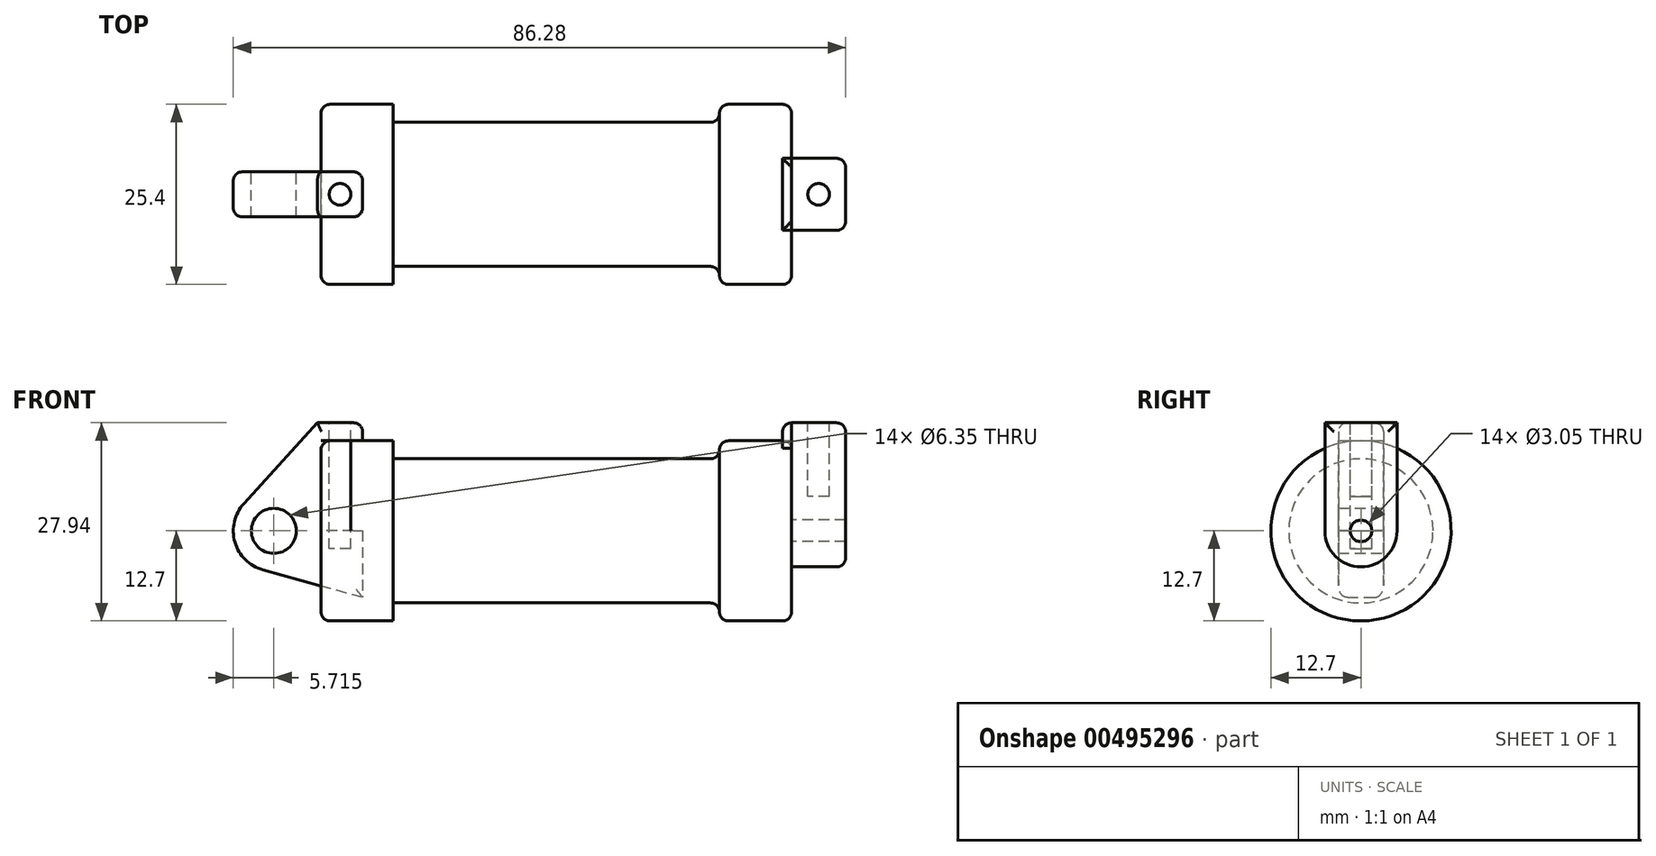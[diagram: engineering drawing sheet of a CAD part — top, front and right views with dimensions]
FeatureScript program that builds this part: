
annotation { "Feature Type Name" : "Feature", "Feature Type Description" : "" }
export const myFeature = defineFeature(function(context is Context, id is Id, definition is map)
    precondition{}
    {
        {
            var Q0;
            Q0=qCreatedBy(makeId("Front.planeOp"),FACE);
            var sketch = newSketch(context, id + "F0", { "sketchPlane" : qUnion([Q0])});
            skLineSegment(sketch, "E0", {"start": v(0, 0) * mm, "end": v(0, 12.7) * mm});
            skLineSegment(sketch, "E1", {"start": v(0, 12.7) * mm, "end": v(10.16, 12.7) * mm});
            skLineSegment(sketch, "E2", {"start": v(10.16, 12.7) * mm, "end": v(10.16, 10.16) * mm});
            skLineSegment(sketch, "E3", {"start": v(10.16, 10.16) * mm, "end": v(56.13, 10.16) * mm});
            skLineSegment(sketch, "E4", {"start": v(56.13, 10.16) * mm, "end": v(56.13, 12.7) * mm});
            skLineSegment(sketch, "E5", {"start": v(56.13, 12.7) * mm, "end": v(66.3, 12.7) * mm});
            skLineSegment(sketch, "E6", {"start": v(66.3, 12.7) * mm, "end": v(66.3, 0) * mm});
            skLineSegment(sketch, "E7", {"start": v(66.3, 0) * mm, "end": v(0, 0) * mm});
            skLineSegment(sketch, "E8", {"start": v(5.84, 15.24) * mm, "end": v(-0.5, 15.24) * mm});
            skLineSegment(sketch, "E9", {"start": v(-0.5, 15.24) * mm, "end": v(-10.88, 3.85) * mm});
            skLineSegment(sketch, "E10", {"start": v(0, 0) * mm, "end": v(-6.65, 0) * mm});
            skCircle(sketch, "E11", {"center": v(-6.65, 0) * mm, "radius": 5.72 * mm});
            skCircle(sketch, "E12", {"center": v(-6.65, 0) * mm, "radius": 3.18 * mm});
            skLineSegment(sketch, "E13", {"start": v(5.84, 15.24) * mm, "end": v(5.84, -9.4) * mm});
            skLineSegment(sketch, "E14", {"start": v(5.84, -9.4) * mm, "end": v(-8.18, -5.5) * mm});
            skSolve(sketch);
        }
        {
            var Q0;
            {var subQ0=sQuery(id+"F0.wireOp",EDGE,"E2");Q0=makeQuery(id+"F0.imprint","IMPRINT",FACE,{"disambiguationData":[TD([[makeQuery(id+"F0.imprint","IMPRINT",EDGE,{"derivedFrom":subQ0}),-1.0]])]});}
            var Q1;
            {var subQ0=sQuery(id+"F0.wireOp",EDGE,"E0");Q1=makeQuery(id+"F0.imprint","IMPRINT",FACE,{"disambiguationData":[TD([[makeQuery(id+"F0.imprint","IMPRINT",EDGE,{"derivedFrom":subQ0}),-1.0]])]});}
            var Q2;
            Q2=sQuery(id+"F0.wireOp",EDGE,"E7");
            revolve(context, id + "F1", {"entities" : qUnion([Q0, Q1]), "axis" : qUnion([Q2]), "revolveType" : RevolveType.FULL});
        }
        {
            var Q0;
            {var subQ1=sQuery(id+"F0.wireOp",EDGE,"E0");Q0=makeQuery(id+"F0.imprint","IMPRINT",FACE,{"disambiguationData":[TD([[makeQuery(id+"F0.imprint","IMPRINT",EDGE,{"derivedFrom":subQ1}),1.0]])]});}
            var Q1;
            {var subQ0=sQuery(id+"F0.wireOp",EDGE,"E14");Q1=makeQuery(id+"F0.imprint","IMPRINT",FACE,{"disambiguationData":[TD([[makeQuery(id+"F0.imprint","IMPRINT",EDGE,{"derivedFrom":subQ0}),-1.0]])]});}
            var Q2;
            {var subQ5=sQuery(id+"F0.wireOp",EDGE,"E12");Q2=makeQuery(id+"F0.imprint","IMPRINT",FACE,{"disambiguationData":[TD([[makeQuery(id+"F0.imprint","IMPRINT",EDGE,{"derivedFrom":subQ5}),-1.0]])]});}
            extrude(context, id + "F2", {"entities" : qUnion([Q0, Q1, Q2]), "endBound" : BoundingType.SYMMETRIC, "depth" : 6.35 * mm});
        }
        {
            var Q0;
            Q0=makeQuery(id+"F1.opRevolve","SWEPT_FACE",FACE,{"disambiguationData":[OSD([sQuery(id+"F0.wireOp",EDGE,"E6")])]});
            var sketch = newSketch(context, id + "F3", { "sketchPlane" : qUnion([Q0])});
            skCircle(sketch, "E15", {"center": v(0, 0) * mm, "radius": 1.52 * mm});
            skCircle(sketch, "E16", {"center": v(0, 0) * mm, "radius": 5.08 * mm});
            skLineSegment(sketch, "E17", {"start": v(-12.7, 0) * mm, "end": v(12.7, 0) * mm, "construction": true});
            skPoint(sketch, "E18", {"position": v(5.08, 0) * mm});
            skPoint(sketch, "E19", {"position": v(-5.08, 0) * mm});
            skLineSegment(sketch, "E20", {"start": v(5.08, 0) * mm, "end": v(5.08, 15.24) * mm});
            skLineSegment(sketch, "E21", {"start": v(-5.08, 0) * mm, "end": v(-5.08, 15.24) * mm});
            skLineSegment(sketch, "E22", {"start": v(-5.08, 15.24) * mm, "end": v(5.08, 15.24) * mm});
            skSolve(sketch);
        }
        {
            var Q0;
            Q0 = qSketchRegion(id + "F3", true);
            extrude(context, id + "F4", {"entities" : qUnion([Q0]), "depth" : 7.62 * mm});
        }
        {
            var Q0;
            {var subQ0=sQuery(id+"F3.wireOp",EDGE,"E22");Q0=makeQuery(id+"F3.imprint","IMPRINT",FACE,{"disambiguationData":[TD([[makeQuery(id+"F3.imprint","IMPRINT",EDGE,{"derivedFrom":subQ0}),-1.0]])]});}
            extrude(context, id + "F5", {"entities" : qUnion([Q0]), "oppositeDirection" : true, "depth" : 1.27 * mm});
        }
        {
            var Q0;
            Q0=makeQuery(id+"F4.opExtrude","SWEPT_FACE",FACE,{"disambiguationData":[OSD([sQuery(id+"F3.wireOp",EDGE,"E22")])]});
            var sketch = newSketch(context, id + "F6", { "sketchPlane" : qUnion([Q0])});
            skLineSegment(sketch, "E23", {"start": v(70.1, 5.08) * mm, "end": v(70.1, -5.08) * mm, "construction": true});
            skPoint(sketch, "E24", {"position": v(70.1, 0) * mm});
            skCircle(sketch, "E25", {"center": v(70.1, 0) * mm, "radius": 1.52 * mm});
            skSolve(sketch);
        }
        {
            var Q0;
            Q0=makeQuery(id+"F6.imprint","IMPRINT",FACE,{"disambiguationData":[TD([[makeQuery(id+"F6.imprint","IMPRINT",EDGE,{"derivedFrom":sQuery(id+"F6.wireOp",EDGE,"E25")}),1.0]])]});
            var Q1;
            Q1=sQuery(id+"F6.wireOp",EDGE,"E25");
            extrude(context, id + "F7", {"entities" : qUnion([Q0]), "surfaceEntities" : qUnion([Q1]), "oppositeDirection" : true, "depth" : 10.4 * mm});
        }
        {
            var Q0;
            Q0=makeQuery(id+"F2.opExtrude","SWEPT_FACE",FACE,{"disambiguationData":[OSD([sQuery(id+"F0.wireOp",EDGE,"E8")])]});
            var sketch = newSketch(context, id + "F8", { "sketchPlane" : qUnion([Q0])});
            skLineSegment(sketch, "E26", {"start": v(-0.5, 3.18) * mm, "end": v(5.84, -3.18) * mm, "construction": true});
            skPoint(sketch, "E27", {"position": v(2.67, 0) * mm});
            skCircle(sketch, "E28", {"center": v(2.67, 0) * mm, "radius": 1.52 * mm});
            skSolve(sketch);
        }
        {
            var Q0;
            Q0=makeQuery(id+"F8.imprint","IMPRINT",FACE,{"disambiguationData":[TD([[makeQuery(id+"F8.imprint","IMPRINT",EDGE,{"derivedFrom":sQuery(id+"F8.wireOp",EDGE,"E28")}),1.0]])]});
            var Q1;
            Q1=sQuery(id+"F8.wireOp",EDGE,"E28");
            extrude(context, id + "F9", {"entities" : qUnion([Q0]), "surfaceEntities" : qUnion([Q1]), "oppositeDirection" : true, "depth" : 17.78 * mm});
        }
        {
            var Q0;
            Q0=makeQuery(id+"F1.opRevolve","SWEPT_FACE",FACE,{"disambiguationData":[OSD([sQuery(id+"F0.wireOp",EDGE,"E6")])]});
            var Q1;
            Q1=makeQuery(id+"F1.opRevolve","SWEPT_FACE",FACE,{"disambiguationData":[OSD([sQuery(id+"F0.wireOp",EDGE,"E0")])]});
            var Q2;
            Q2=makeQuery(id+"F1.opRevolve","SWEPT_FACE",FACE,{"disambiguationData":[OSD([sQuery(id+"F0.wireOp",EDGE,"E4")])]});
            var Q3;
            Q3=makeQuery(id+"F4.opExtrude","CAP_EDGE",EDGE,{"disambiguationData":[OSD([sQuery(id+"F3.wireOp",EDGE,"E20")])],"isStart":false});
            var Q4;
            {var subQ0=sQuery(id+"F3.wireOp",EDGE,"E22");Q4=makeQuery(id+"F7.opExtrude","CAP_EDGE",EDGE,{"disambiguationData":[OSD([subQ0]),TDD([makeQuery(id+"F6.imprint","IMPRINT",EDGE,{"derivedFrom":makeQuery(id+"F4.opExtrude","CAP_EDGE",EDGE,{"disambiguationData":[OSD([subQ0])],"isStart":false})})])],"isStart":true});}
            var Q5;
            Q5=makeQuery(id+"F7.opExtrude","CAP_EDGE",EDGE,{"disambiguationData":[OSD([sQuery(id+"F3.wireOp",EDGE,"E21"),sQuery(id+"F3.wireOp",EDGE,"E22")])],"isStart":true});
            var Q6;
            Q6=makeQuery(id+"F7.opExtrude","CAP_EDGE",EDGE,{"disambiguationData":[OSD([sQuery(id+"F3.wireOp",EDGE,"E20"),sQuery(id+"F3.wireOp",EDGE,"E22")])],"isStart":true});
            var Q7;
            Q7=makeQuery(id+"F5.opExtrude","CAP_EDGE",EDGE,{"disambiguationData":[OSD([sQuery(id+"F3.wireOp",EDGE,"E22")])],"isStart":false});
            var Q8;
            Q8=makeQuery(id+"F5.opExtrude","SWEPT_EDGE",EDGE,{"disambiguationData":[OSD([sQuery(id+"F3.wireOp",EDGE,"E21"),sQuery(id+"F3.wireOp",EDGE,"E22")])]});
            var Q9;
            Q9=makeQuery(id+"F5.opExtrude","SWEPT_EDGE",EDGE,{"disambiguationData":[OSD([sQuery(id+"F3.wireOp",EDGE,"E20"),sQuery(id+"F3.wireOp",EDGE,"E22")])]});
            var Q10;
            Q10=makeQuery(id+"F2.opExtrude","CAP_EDGE",EDGE,{"disambiguationData":[OSD([sQuery(id+"F0.wireOp",EDGE,"E11")])],"isStart":true});
            var Q11;
            Q11=makeQuery(id+"F2.opExtrude","CAP_EDGE",EDGE,{"disambiguationData":[OSD([sQuery(id+"F0.wireOp",EDGE,"E9")])],"isStart":true});
            var Q12;
            Q12=makeQuery(id+"F2.opExtrude","CAP_EDGE",EDGE,{"disambiguationData":[OSD([sQuery(id+"F0.wireOp",EDGE,"E9")])],"isStart":false});
            var Q13;
            Q13=makeQuery(id+"F2.opExtrude","CAP_EDGE",EDGE,{"disambiguationData":[OSD([sQuery(id+"F0.wireOp",EDGE,"E11")])],"isStart":false});
            var Q14;
            Q14=makeQuery(id+"F2.opExtrude","CAP_EDGE",EDGE,{"disambiguationData":[OSD([sQuery(id+"F0.wireOp",EDGE,"E8")])],"isStart":true});
            var Q15;
            Q15=makeQuery(id+"F2.opExtrude","CAP_EDGE",EDGE,{"disambiguationData":[OSD([sQuery(id+"F0.wireOp",EDGE,"E8")])],"isStart":false});
            var Q16;
            Q16=makeQuery(id+"F2.opExtrude","SWEPT_EDGE",EDGE,{"disambiguationData":[OSD([sQuery(id+"F0.wireOp",EDGE,"E8"),sQuery(id+"F0.wireOp",EDGE,"E13")])]});
            var Q17;
            {var subQ0=sQuery(id+"F0.wireOp",EDGE,"E8");var subQ1=sQuery(id+"F0.wireOp",EDGE,"E13");Q17=makeQuery(id+"F9.boolean.opBoolean","MERGE",EDGE,{"derivedFrom":[makeQuery(id+"F2.opExtrude","CAP_EDGE",EDGE,{"disambiguationData":[OSD([subQ1]),TDD([makeQuery(id+"F0.imprint","IMPRINT",EDGE,{"disambiguationData":[TD([[makeQuery(id+"F0.imprint","INTERSECT",VERTEX,{"derivedFrom":[subQ0,subQ1]}),-1.0]])],"derivedFrom":subQ1})])],"isStart":false}),makeQuery(id+"F2.opExtrude","CAP_EDGE",EDGE,{"disambiguationData":[OSD([subQ1]),TDD([makeQuery(id+"F0.imprint","IMPRINT",EDGE,{"disambiguationData":[TD([[makeQuery(id+"F0.imprint","INTERSECT",VERTEX,{"derivedFrom":[subQ1,sQuery(id+"F0.wireOp",EDGE,"E14")]}),1.0]])],"derivedFrom":subQ1})])],"isStart":false}),makeQuery(id+"F9.opExtrude","SWEPT_EDGE",EDGE,{"disambiguationData":[OSD([subQ0,subQ1]),TDD([makeQuery(id+"F8.imprint","INTERSECT",VERTEX,{"derivedFrom":[makeQuery(id+"F2.opExtrude","SWEPT_EDGE",EDGE,{"disambiguationData":[OSD([subQ0,subQ1])]}),makeQuery(id+"F2.opExtrude","CAP_EDGE",EDGE,{"disambiguationData":[OSD([subQ0])],"isStart":false})]})])]})]});}
            var Q18;
            {var subQ0=sQuery(id+"F0.wireOp",EDGE,"E8");var subQ1=sQuery(id+"F0.wireOp",EDGE,"E13");Q18=makeQuery(id+"F9.boolean.opBoolean","MERGE",EDGE,{"derivedFrom":[makeQuery(id+"F2.opExtrude","CAP_EDGE",EDGE,{"disambiguationData":[OSD([subQ1]),TDD([makeQuery(id+"F0.imprint","IMPRINT",EDGE,{"disambiguationData":[TD([[makeQuery(id+"F0.imprint","INTERSECT",VERTEX,{"derivedFrom":[subQ0,subQ1]}),-1.0]])],"derivedFrom":subQ1})])],"isStart":true}),makeQuery(id+"F2.opExtrude","CAP_EDGE",EDGE,{"disambiguationData":[OSD([subQ1]),TDD([makeQuery(id+"F0.imprint","IMPRINT",EDGE,{"disambiguationData":[TD([[makeQuery(id+"F0.imprint","INTERSECT",VERTEX,{"derivedFrom":[subQ1,sQuery(id+"F0.wireOp",EDGE,"E14")]}),1.0]])],"derivedFrom":subQ1})])],"isStart":true}),makeQuery(id+"F9.opExtrude","SWEPT_EDGE",EDGE,{"disambiguationData":[OSD([subQ0,subQ1]),TDD([makeQuery(id+"F8.imprint","INTERSECT",VERTEX,{"derivedFrom":[makeQuery(id+"F2.opExtrude","SWEPT_EDGE",EDGE,{"disambiguationData":[OSD([subQ0,subQ1])]}),makeQuery(id+"F2.opExtrude","CAP_EDGE",EDGE,{"disambiguationData":[OSD([subQ0])],"isStart":true})]})])]})]});}
            var Q19;
            Q19=makeQuery(id+"F4.opExtrude","CAP_EDGE",EDGE,{"disambiguationData":[OSD([sQuery(id+"F3.wireOp",EDGE,"E22")])],"isStart":false});
            fillet(context, id + "F10", {"entities" : qUnion([Q0, Q1, Q2, Q3, Q4, Q5, Q6, Q7, Q8, Q9, Q10, Q11, Q12, Q13, Q14, Q15, Q16, Q17, Q18, Q19]), "radius" : 1.27 * mm, "tangentPropagation" : true, "allowEdgeOverflow" : false});
        }
    });
